# Revit family: Haworth_Compose_Panel_StackFramelessGlass
name_source: partatom
category: Furniture Systems
revit_build: Autodesk Revit 2018 (Build: 20170223_1515(x64)
units: mm (PartAtom-declared; Revit-internal decimal feet)

## family parameters
Always vertical = Yes
Cut with Voids When Loaded = No
OmniClass Number = 23.40.70.14.64.21
OmniClass Title = Systems Furniture
Part Type = Normal
Room Calculation Point = No
Round Connector Dimension = Use Diameter
Shared = No
Work Plane-Based = No

## types (96) — shared parameters
Assembly Code = E2020500
Depth = 2 5/16"
Description = Haworth - Compose Panel Glass - Frameless Glass
Glass Finish = Haworth _ Glass _ Clear
Manufacturer = Haworth
Max. Height = 16"
Max. Width = 120"
Min. Height = 8"
Min. Width = 18"
Min/Max Height = 8, 12, 16 in.
Min/Max Width = 18, 24, 30, 36-120 in. @ 3 in. Increments
Model = VZGK
Revision Number = 4
Size = Verify Final Dim. w/ Haworth
Sustainability Info = http://media.haworth.com
Trim Finish = Haworth _ Paint _ Putty
Trim Height = 3/8"
URL = http://www.haworth.com
URL - Product = http://www.haworth.com
Warranty = http://www.haworth.com

## per-type parameters (varying)
| type | Actual Height | Actual Width | Custom Size | Height | Panel Width | Width |
| 8h 18w | 8" | 18" | Yes | 8" | 17 3/4" | 18" |
| 8h 24w | 8" | 24" | No | 8" | 23 3/4" | 24" |
| 8h 30w | 8" | 30" | No | 8" | 29 3/4" | 30" |
| 8h 36w | 8" | 36" | No | 8" | 35 3/4" | 36" |
| 8h 39w | 8" | 39" | No | 8" | 38 3/4" | 39" |
| 8h 42w | 8" | 42" | No | 8" | 41 3/4" | 42" |
| 8h 45w | 8" | 45" | No | 8" | 44 3/4" | 45" |
| 8h 48w | 8" | 48" | No | 8" | 47 3/4" | 48" |
| 8h 51w | 8" | 51" | No | 8" | 50 3/4" | 51" |
| 8h 54w | 8" | 54" | No | 8" | 53 3/4" | 54" |
| 8h 57w | 8" | 57" | No | 8" | 56 3/4" | 57" |
| 8h 60w | 8" | 60" | No | 8" | 59 3/4" | 60" |
| 8h 63w | 8" | 63" | No | 8" | 62 3/4" | 63" |
| 8h 66w | 8" | 66" | No | 8" | 65 3/4" | 66" |
| 8h 69w | 8" | 69" | No | 8" | 68 3/4" | 69" |
| 8h 72w | 8" | 72" | No | 8" | 71 3/4" | 72" |
| 8h 75w | 8" | 75" | No | 8" | 74 3/4" | 75" |
| 8h 78w | 8" | 78" | No | 8" | 77 3/4" | 78" |
| 8h 81w | 8" | 81" | No | 8" | 80 3/4" | 81" |
| 8h 84w | 8" | 84" | No | 8" | 83 3/4" | 84" |
| 8h 87w | 8" | 87" | No | 8" | 86 3/4" | 87" |
| 8h 90w | 8" | 90" | No | 8" | 89 3/4" | 90" |
| 8h 93w | 8" | 93" | No | 8" | 92 3/4" | 93" |
| 8h 96w | 8" | 96" | No | 8" | 95 3/4" | 96" |
| 8h 99w | 8" | 99" | No | 8" | 98 3/4" | 99" |
| 8h 102w | 8" | 102" | No | 8" | 101 3/4" | 102" |
| 8h 105w | 8" | 105" | No | 8" | 104 3/4" | 105" |
| 8h 108w | 8" | 108" | No | 8" | 107 3/4" | 108" |
| 8h 111w | 8" | 111" | No | 8" | 110 3/4" | 111" |
| 8h 114w | 8" | 114" | No | 8" | 113 3/4" | 114" |
| 8h 117w | 8" | 117" | No | 8" | 116 3/4" | 117" |
| 8h 120w | 8" | 120" | No | 8" | 119 3/4" | 120" |
| 12h 18w | 12" | 18" | Yes | 12" | 17 3/4" | 18" |
| 12h 24w | 12" | 24" | No | 12" | 23 3/4" | 24" |
| 12h 30w | 12" | 30" | No | 12" | 29 3/4" | 30" |
| 12h 36w | 12" | 36" | No | 12" | 35 3/4" | 36" |
| 12h 39w | 12" | 39" | No | 12" | 38 3/4" | 39" |
| 12h 42w | 12" | 42" | No | 12" | 41 3/4" | 42" |
| 12h 45w | 12" | 45" | No | 12" | 44 3/4" | 45" |
| 12h 48w | 12" | 48" | No | 12" | 47 3/4" | 48" |
| 12h 51w | 12" | 51" | No | 12" | 50 3/4" | 51" |
| 12h 54w | 12" | 54" | No | 12" | 53 3/4" | 54" |
| 12h 57w | 12" | 57" | No | 12" | 56 3/4" | 57" |
| 12h 60w | 12" | 60" | No | 12" | 59 3/4" | 60" |
| 12h 63w | 12" | 63" | No | 12" | 62 3/4" | 63" |
| 12h 66w | 12" | 66" | No | 12" | 65 3/4" | 66" |
| 12h 69w | 12" | 69" | No | 12" | 68 3/4" | 69" |
| 12h 72w | 12" | 72" | No | 12" | 71 3/4" | 72" |
| 12h 75w | 12" | 75" | No | 12" | 74 3/4" | 75" |
| 12h 78w | 12" | 78" | No | 12" | 77 3/4" | 78" |
| 12h 81w | 12" | 81" | No | 12" | 80 3/4" | 81" |
| 12h 84w | 12" | 84" | No | 12" | 83 3/4" | 84" |
| 12h 87w | 12" | 87" | No | 12" | 86 3/4" | 87" |
| 12h 90w | 12" | 90" | No | 12" | 89 3/4" | 90" |
| 12h 93w | 12" | 93" | No | 12" | 92 3/4" | 93" |
| 12h 96w | 12" | 96" | No | 12" | 95 3/4" | 96" |
| 12h 99w | 12" | 99" | No | 12" | 98 3/4" | 99" |
| 12h 102w | 12" | 102" | No | 12" | 101 3/4" | 102" |
| 12h 105w | 12" | 105" | No | 12" | 104 3/4" | 105" |
| 12h 108w | 12" | 108" | No | 12" | 107 3/4" | 108" |
| 12h 111w | 12" | 111" | No | 12" | 110 3/4" | 111" |
| 12h 114w | 12" | 114" | No | 12" | 113 3/4" | 114" |
| 12h 117w | 12" | 117" | No | 12" | 116 3/4" | 117" |
| 12h 120w | 12" | 120" | No | 12" | 119 3/4" | 120" |
| 16h 18w | 16" | 18" | Yes | 16" | 17 3/4" | 18" |
| 16h 24w | 16" | 24" | No | 16" | 23 3/4" | 24" |
| 16h 30w | 16" | 30" | No | 16" | 29 3/4" | 30" |
| 16h 36w | 16" | 36" | No | 16" | 35 3/4" | 36" |
| 16h 39w | 16" | 39" | No | 16" | 38 3/4" | 39" |
| 16h 42w | 16" | 42" | No | 16" | 41 3/4" | 42" |
| 16h 45w | 16" | 45" | No | 16" | 44 3/4" | 45" |
| 16h 48w | 16" | 48" | No | 16" | 47 3/4" | 48" |
| 16h 51w | 16" | 51" | No | 16" | 50 3/4" | 51" |
| 16h 54w | 16" | 54" | No | 16" | 53 3/4" | 54" |
| 16h 57w | 16" | 57" | No | 16" | 56 3/4" | 57" |
| 16h 60w | 16" | 60" | No | 16" | 59 3/4" | 60" |
| 16h 63w | 16" | 63" | No | 16" | 62 3/4" | 63" |
| 16h 66w | 16" | 66" | No | 16" | 65 3/4" | 66" |
| 16h 69w | 16" | 69" | No | 16" | 68 3/4" | 69" |
| 16h 72w | 16" | 72" | No | 16" | 71 3/4" | 72" |
| 16h 75w | 16" | 75" | No | 16" | 74 3/4" | 75" |
| 16h 78w | 16" | 78" | No | 16" | 77 3/4" | 78" |
| 16h 81w | 16" | 81" | No | 16" | 80 3/4" | 81" |
| 16h 84w | 16" | 84" | No | 16" | 83 3/4" | 84" |
| 16h 87w | 16" | 87" | No | 16" | 86 3/4" | 87" |
| 16h 90w | 16" | 90" | No | 16" | 89 3/4" | 90" |
| 16h 93w | 16" | 93" | No | 16" | 92 3/4" | 93" |
| 16h 96w | 16" | 96" | No | 16" | 95 3/4" | 96" |
| 16h 99w | 16" | 99" | No | 16" | 98 3/4" | 99" |
| 16h 102w | 16" | 102" | No | 16" | 101 3/4" | 102" |
| 16h 105w | 16" | 105" | No | 16" | 104 3/4" | 105" |
| 16h 108w | 16" | 108" | No | 16" | 107 3/4" | 108" |
| 16h 111w | 16" | 111" | No | 16" | 110 3/4" | 111" |
| 16h 114w | 16" | 114" | No | 16" | 113 3/4" | 114" |
| 16h 117w | 16" | 117" | No | 16" | 116 3/4" | 117" |
| 16h 120w | 16" | 120" | No | 16" | 119 3/4" | 120" |

## geometry (parser evidence)
native form markers: Sweep x3
no freeform markers — native parametric forms only
